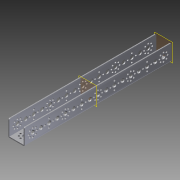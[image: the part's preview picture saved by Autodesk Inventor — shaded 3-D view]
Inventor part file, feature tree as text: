
AUTODESK INVENTOR PART (.ipt)
format: ipt  version: 2013 (Build 170138000, 138)  size: 477,184 bytes
history: native  units: in
note: dims shown in document units (in); Inventor stores cm internally (conversion verified against a paired STEP export)
features: plane x2, other x1, imported_body x1, move_body x1
ambient origin geometry x8: Origin, YZ Plane, XZ Plane, XY Plane, X Axis, Y Axis, Z Axis, Center Point
feature tree (5):
  other  "CHANNEL_288_2011"
  imported_body  "Base1"
  move_body  "Move Body1"
  plane  "Work Plane1"
  plane  "Work Plane2"
